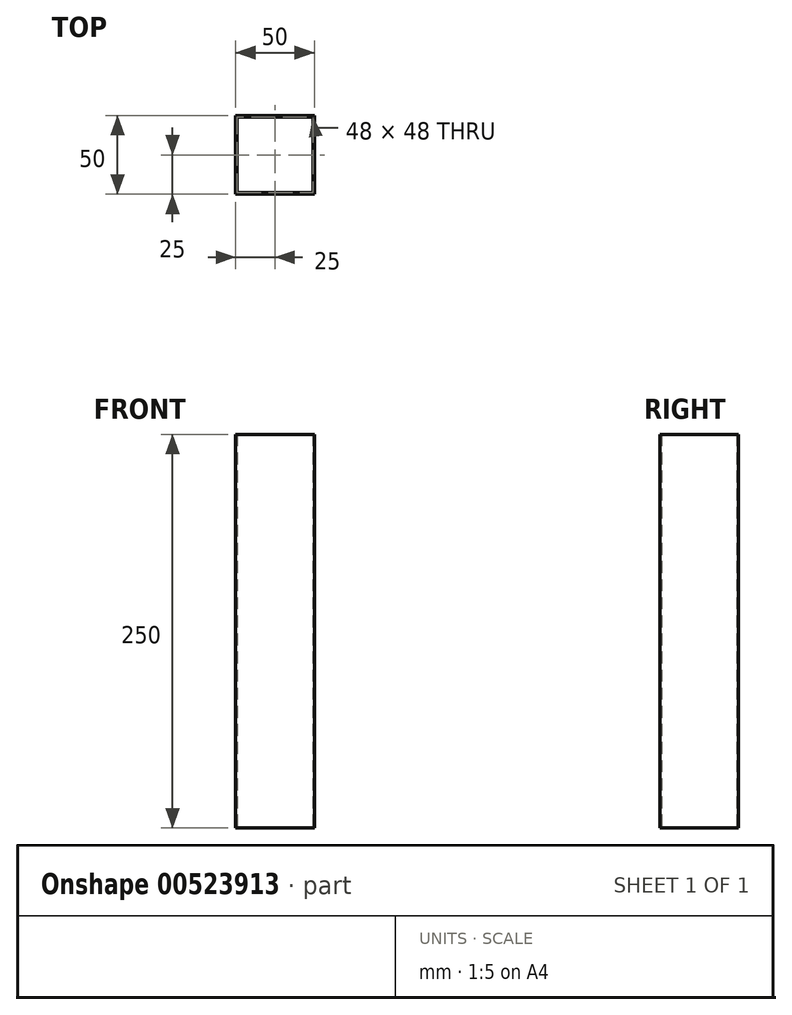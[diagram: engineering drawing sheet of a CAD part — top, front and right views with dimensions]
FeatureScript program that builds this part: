
annotation { "Feature Type Name" : "Feature", "Feature Type Description" : "" }
export const myFeature = defineFeature(function(context is Context, id is Id, definition is map)
    precondition{}
    {
        {
            var Q0;
            Q0=qCreatedBy(makeId("Top.planeOp"),FACE);
            var sketch = newSketch(context, id + "F0", { "sketchPlane" : qUnion([Q0])});
            skLineSegment(sketch, "E0.bottom", {"start": v(25, 25) * mm, "end": v(-25, 25) * mm});
            skLineSegment(sketch, "E0.top", {"start": v(25, -25) * mm, "end": v(-25, -25) * mm});
            skLineSegment(sketch, "E0.left", {"start": v(25, 25) * mm, "end": v(25, -25) * mm});
            skLineSegment(sketch, "E0.right", {"start": v(-25, 25) * mm, "end": v(-25, -25) * mm});
            skPoint(sketch, "E0.middle", {"position": v(0, 0) * mm});
            skLineSegment(sketch, "E1.bottom", {"start": v(24, 24) * mm, "end": v(-24, 24) * mm});
            skLineSegment(sketch, "E1.top", {"start": v(24, -24) * mm, "end": v(-24, -24) * mm});
            skLineSegment(sketch, "E1.left", {"start": v(24, 24) * mm, "end": v(24, -24) * mm});
            skLineSegment(sketch, "E1.right", {"start": v(-24, 24) * mm, "end": v(-24, -24) * mm});
            skSolve(sketch);
        }
        {
            var Q0;
            Q0=makeQuery(id+"F0.imprint","IMPRINT",FACE,{"disambiguationData":[TD([[makeQuery(id+"F0.imprint","IMPRINT",EDGE,{"derivedFrom":sQuery(id+"F0.wireOp",EDGE,"E0.bottom")}),1.0]])]});
            extrude(context, id + "F1", {"entities" : qUnion([Q0]), "depth" : 250 * mm, "offsetDistance" : 25 * mm});
        }
    });
